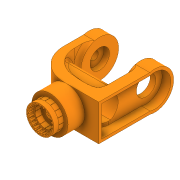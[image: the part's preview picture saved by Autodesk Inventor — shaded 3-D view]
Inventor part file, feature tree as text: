
AUTODESK INVENTOR PART (.ipt)
format: ipt  version: 2020 (Build 240168000, 168)  size: 1,530,880 bytes
history: native  units: in
note: dims shown in document units (in); Inventor stores cm internally (conversion verified against a paired STEP export)
features: sketch x30, extrude x29, projected_geometry x25, plane x4, chamfer x3, fillet x3
ambient origin geometry x8: Origin, YZ Plane, XZ Plane, XY Plane, X Axis, Y Axis, Z Axis, Center Point
bodies: Solid1 (feature_tree)
feature tree (94):
  extrude  "Extrusion1"  Depth=2.0472in
  extrude  "Extrusion2"  Depth=1.1024in
  chamfer  "Chamfer2"  Distance=0.2756in
  extrude  "Extrusion4"  Depth=0.0157in
  extrude  "Extrusion7"  Depth=0.2756in TaperAngle=0.0deg
  chamfer  "Chamfer4"  Distance=0.0394in
  extrude  "Extrusion8"  Depth=0.0157in
  sketch  "Sketch12"  dims[d39=1.4567in d57=0.0394in d58=0.0in]
  plane  "Work Plane1"
  sketch  "Sketch13"  dims[d59=0.315in d60=0.125in d61=0.0137in d67=0.0157in]
  extrude  "Extrusion10"  Depth=0.0394in TaperAngle=0.0deg
  extrude  "Extrusion11"  Depth=0.0866in
  chamfer  "Chamfer5"  Distance=9.4488in Angle=360.0deg
  extrude  "Extrusion12"  Depth=0.2756in TaperAngle=0.0deg
  plane  "Work Plane2"
  extrude  "Extrusion13"  Depth=0.2756in
  plane  "Work Plane3"
  extrude  "Extrusion14"  Depth=1.0236in
  extrude  "Extrusion15"  Depth=0.8858in
  extrude  "Extrusion16"  Depth=0.3937in
  extrude  "Extrusion17"  Depth=1.378in
  sketch  "Sketch21"  dims[d107=0.2756in d108=0.0in d109=0.2756in d110=0.125in d111=0.0137in]
  extrude  "Extrusion19"  Depth=0.5906in
  sketch  "Sketch23"  dims[d112=1.0in d113=0.0in d114=1.0236in]
  extrude  "Extrusion20"  Depth=0.1575in TaperAngle=0.0deg
  extrude  "Extrusion21"  Depth=0.1575in TaperAngle=0.0deg
  extrude  "Extrusion22"  Depth=4.2323in
  extrude  "Extrusion23"  Depth=0.1575in
  extrude  "Extrusion24"  Depth=1.1024in
  extrude  "Extrusion25"  Depth=0.4921in
  extrude  "Extrusion26"  Depth=0.75in
  extrude  "Extrusion27"  Depth=0.1575in TaperAngle=0.0deg
  extrude  "Extrusion28"  Depth=0.1575in
  extrude  "Extrusion29"  Depth=0.1575in
  plane  "Work Plane4"
  extrude  "Extrusion30"  Depth=0.1575in TaperAngle=0.0deg
  fillet  "Fillet1"  Radius=0.315in
  fillet  "Fillet2"  Radius=0.3937in
  extrude  "Extrusion31"  Depth=0.1575in TaperAngle=0.0deg
  extrude  "Extrusion32"  Depth=0.1575in TaperAngle=0.0deg
  extrude  "Extrusion33"  Depth=0.1575in TaperAngle=0.0deg
  fillet  "Fillet3"  Radius=0.315in
  extrude  "Extrusion34"  Depth=0.1575in TaperAngle=0.0deg
  sketch  "Sketch1"  dims[d0=0.6299in d1=2.0472in]
  sketch  "Sketch2"  dims[d2=0.9449in d3=0.0in d4=1.1024in]
  sketch  "Sketch4"  dims[d5=1.5748in d6=0.2756in d7=0.0in]
  sketch  "Sketch8"  dims[d11=0.2756in d12=0.125in d13=0.0137in d25=0.0157in]
  projected_geometry  "Projected Loop2"
  sketch  "Sketch10"  dims[d26=6.2992in d28=360.0deg d30=0.2756in d31=0.0in]
  sketch  "Sketch14"  dims[d68=4.7244in d70=360.0deg d72=0.0394in d73=0.0in]
  sketch  "Sketch15"  dims[d83=0.0591in d84=0.0866in]
  projected_geometry  "Projected Loop4"
  sketch  "Sketch16"  dims[d85=0.0827in]
  sketch  "Sketch17"  dims[d86=0.0827in]
  projected_geometry  "Projected Loop5"
  sketch  "Sketch18"  dims[d87=0.0827in d88=9.4488in d90=360.0deg]
  projected_geometry  "Projected Loop6"
  projected_geometry  "Projected Loop7"
  sketch  "Sketch19"  dims[d92=0.2756in]
  projected_geometry  "Projected Loop8"
  projected_geometry  "Projected Loop9"
  sketch  "Sketch20"  dims[d94=9.4488in d95=0.0827in d96=0.0827in d97=0.0827in d98=360.0deg d105=0.2756in d106=0.0in]
  projected_geometry  "Projected Loop10"
  projected_geometry  "Projected Loop11"
  projected_geometry  "Projected Loop12"
  projected_geometry  "Projected Loop13"
  sketch  "Sketch25"  dims[d115=0.7874in d117=0.8858in]
  sketch  "Sketch26"  dims[d118=2.7559in d119=0.3937in]
  projected_geometry  "Projected Loop16"
  projected_geometry  "Projected Loop17"
  sketch  "Sketch27"  dims[d120=0.5906in d121=1.378in]
  projected_geometry  "Projected Loop18"
  projected_geometry  "Projected Loop19"
  sketch  "Sketch28"  dims[d123=3.4941in d124=0.5906in]
  projected_geometry  "Projected Loop20"
  projected_geometry  "Projected Loop21"
  sketch  "Sketch29"  dims[d126=1.9685in d129=0.1575in d130=0.0in]
  projected_geometry  "Projected Loop22"
  projected_geometry  "Projected Loop23"
  sketch  "Sketch30"  dims[d131=-2.0472in d132=0.1575in d133=0.0in]
  projected_geometry  "Projected Loop24"
  sketch  "Sketch31"  dims[d134=2.126in d136=4.2323in]
  sketch  "Sketch32"  dims[d137=0.1575in d138=0.1575in]
  sketch  "Sketch34"  dims[d139=0.4921in d140=0.0in d141=1.1024in]
  projected_geometry  "Projected Loop25"
  sketch  "Sketch35"  dims[d142=1.1614in d143=0.4921in]
  sketch  "Sketch36"  dims[d144=0.3445in d145=0.75in]
  projected_geometry  "Projected Loop26"
  sketch  "Sketch37"  dims[d146=0.1575in d147=0.0in d148=0.2165in d149=0.0in]
  projected_geometry  "Projected Loop27"
  sketch  "Sketch38"  dims[d152=1.0039in d153=0.0in d154=0.1575in]
  projected_geometry  "Projected Loop28"
  sketch  "Sketch39"  dims[d155=0.1575in d160=1.1811in d161=0.1969in d162=0.0in d163=0.315in d164=0.0in d165=0.3937in d166=0.0in d167=0.315in d168=0.0in d169=0.315in d170=0.0in d171=0.315in d172=0.0in d173=0.315in d174=0.0in d175=0.315in d176=0.0in d177=1.1024in d178=0.3937in d179=0.0in d180=0.2165in d181=0.0in d183=-0.0197in d184=0.4724in d185=0.2756in d186=0.0in d187=0.5512in d188=0.2165in d189=0.0394in d190=0.0in d191=0.0394in d192=0.0in d193=0.001in d194=0.001in d195=1.0in d196=0.0in d197=0.1575in d198=1.0in d199=0.0in]
  projected_geometry  "Projected Loop29"
